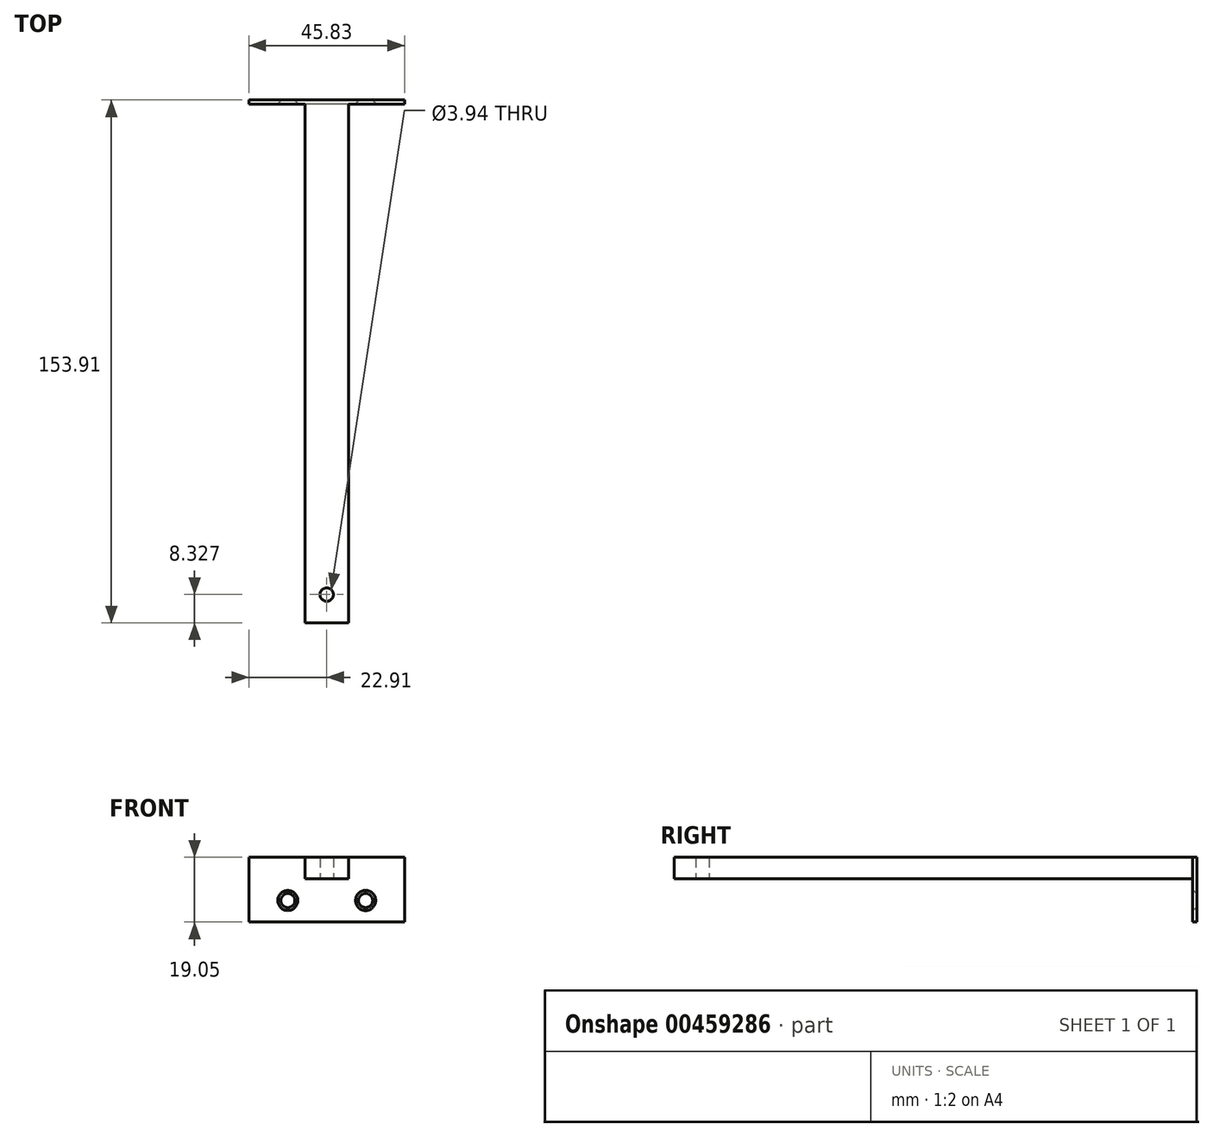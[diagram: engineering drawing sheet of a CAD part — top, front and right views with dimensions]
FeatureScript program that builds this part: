
annotation { "Feature Type Name" : "Feature", "Feature Type Description" : "" }
export const myFeature = defineFeature(function(context is Context, id is Id, definition is map)
    precondition{}
    {
        {
            var Q0;
            Q0=qCreatedBy(makeId("Top.planeOp"),FACE);
            var sketch = newSketch(context, id + "F0", { "sketchPlane" : qUnion([Q0])});
            skLineSegment(sketch, "E0.bottom", {"start": v(6.4, 76.32) * mm, "end": v(-6.4, 76.32) * mm});
            skLineSegment(sketch, "E0.top", {"start": v(6.4, -76.32) * mm, "end": v(-6.4, -76.32) * mm});
            skLineSegment(sketch, "E0.left", {"start": v(6.4, 76.32) * mm, "end": v(6.4, -76.32) * mm});
            skLineSegment(sketch, "E0.right", {"start": v(-6.4, 76.32) * mm, "end": v(-6.4, -76.32) * mm});
            skPoint(sketch, "E0.middle", {"position": v(0, 0) * mm});
            skPoint(sketch, "E1.endSnap0", {"position": v(0, -76.32) * mm});
            skCircle(sketch, "E2", {"center": v(0, -68) * mm, "radius": 1.97 * mm});
            skSolve(sketch);
        }
        {
            var Q0;
            Q0=makeQuery(id+"F0.imprint","IMPRINT",FACE,{"disambiguationData":[TD([[makeQuery(id+"F0.imprint","IMPRINT",EDGE,{"derivedFrom":sQuery(id+"F0.wireOp",EDGE,"E0.bottom")}),1.0]])]});
            extrude(context, id + "F1", {"entities" : qUnion([Q0]), "depth" : 6.35 * mm});
        }
        {
            var Q0;
            Q0=makeQuery(id+"F1.opExtrude","SWEPT_FACE",FACE,{"disambiguationData":[OSD([sQuery(id+"F0.wireOp",EDGE,"E0.bottom")])]});
            var sketch = newSketch(context, id + "F2", { "sketchPlane" : qUnion([Q0])});
            skLineSegment(sketch, "E3", {"start": v(-6.4, 0) * mm, "end": v(-22.92, 0) * mm});
            skLineSegment(sketch, "E4", {"start": v(6.4, 0) * mm, "end": v(22.91, 0) * mm});
            skLineSegment(sketch, "E5", {"start": v(-6.4, 0) * mm, "end": v(6.4, 0) * mm});
            skLineSegment(sketch, "E6", {"start": v(-22.92, 0) * mm, "end": v(-22.92, -12.7) * mm});
            skLineSegment(sketch, "E7", {"start": v(-22.92, -12.7) * mm, "end": v(22.91, -12.7) * mm});
            skLineSegment(sketch, "E8", {"start": v(22.91, -12.7) * mm, "end": v(22.91, 0) * mm});
            skLineSegment(sketch, "E9", {"start": v(-6.4, 6.35) * mm, "end": v(-22.92, 6.35) * mm});
            skLineSegment(sketch, "E10", {"start": v(-22.92, 6.35) * mm, "end": v(-22.92, 0) * mm});
            skLineSegment(sketch, "E11", {"start": v(6.4, 6.35) * mm, "end": v(22.91, 6.35) * mm});
            skLineSegment(sketch, "E12", {"start": v(22.91, 6.35) * mm, "end": v(22.91, 0) * mm});
            skSolve(sketch);
        }
        {
            var Q0;
            Q0=makeQuery(id+"F2.imprint","IMPRINT",FACE,{"disambiguationData":[TD([[makeQuery(id+"F2.imprint","IMPRINT",EDGE,{"derivedFrom":sQuery(id+"F2.wireOp",EDGE,"E5")}),1.0]])]});
            var Q1;
            Q1=makeQuery(id+"F2.imprint","IMPRINT",FACE,{"disambiguationData":[TD([[makeQuery(id+"F2.imprint","IMPRINT",EDGE,{"derivedFrom":sQuery(id+"F2.wireOp",EDGE,"E3")}),-1.0]])]});
            var Q2;
            Q2=makeQuery(id+"F2.imprint","IMPRINT",FACE,{"disambiguationData":[TD([[makeQuery(id+"F2.imprint","IMPRINT",EDGE,{"derivedFrom":sQuery(id+"F2.wireOp",EDGE,"E4")}),1.0]])]});
            var Q3;
            Q3=makeQuery(id+"F2.imprint","IMPRINT",FACE,{"disambiguationData":[TD([[makeQuery(id+"F2.imprint","IMPRINT",EDGE,{"derivedFrom":sQuery(id+"F2.wireOp",EDGE,"E3")}),1.0]])]});
            extrude(context, id + "F3", {"entities" : qUnion([Q0, Q1, Q2, Q3]), "operationType" : NewBodyOperationType.ADD, "depth" : 1.27 * mm});
        }
        {
            var Q0;
            Q0=makeQuery(id+"F3.opExtrude","CAP_FACE",FACE,{"disambiguationData":[OSD([sQuery(id+"F0.wireOp",EDGE,"E0.bottom"),sQuery(id+"F2.wireOp",EDGE,"E6"),sQuery(id+"F2.wireOp",EDGE,"E7"),sQuery(id+"F2.wireOp",EDGE,"E8"),sQuery(id+"F2.wireOp",EDGE,"E9"),sQuery(id+"F2.wireOp",EDGE,"E10"),sQuery(id+"F2.wireOp",EDGE,"E11"),sQuery(id+"F2.wireOp",EDGE,"E12")])],"isStart":true});
            var sketch = newSketch(context, id + "F4", { "sketchPlane" : qUnion([Q0])});
            skCircle(sketch, "E13", {"center": v(11.46, -6.35) * mm, "radius": 2.96 * mm});
            skCircle(sketch, "E14", {"center": v(-11.46, -6.35) * mm, "radius": 2.96 * mm});
            skSolve(sketch);
        }
        {
            var Q0;
            Q0=makeQuery(id+"F4.imprint","IMPRINT",FACE,{"disambiguationData":[TD([[makeQuery(id+"F4.imprint","IMPRINT",EDGE,{"derivedFrom":sQuery(id+"F4.wireOp",EDGE,"E13")}),1.0]])]});
            var Q1;
            Q1=makeQuery(id+"F4.imprint","IMPRINT",FACE,{"disambiguationData":[TD([[makeQuery(id+"F4.imprint","IMPRINT",EDGE,{"derivedFrom":sQuery(id+"F4.wireOp",EDGE,"E14")}),1.0]])]});
            extrude(context, id + "F5", {"entities" : qUnion([Q0, Q1]), "operationType" : NewBodyOperationType.REMOVE, "oppositeDirection" : true, "depth" : 1.27 * mm, "hasDraft" : true, "draftAngle" : 35 * degree, "draftPullDirection" : true});
        }
    });
